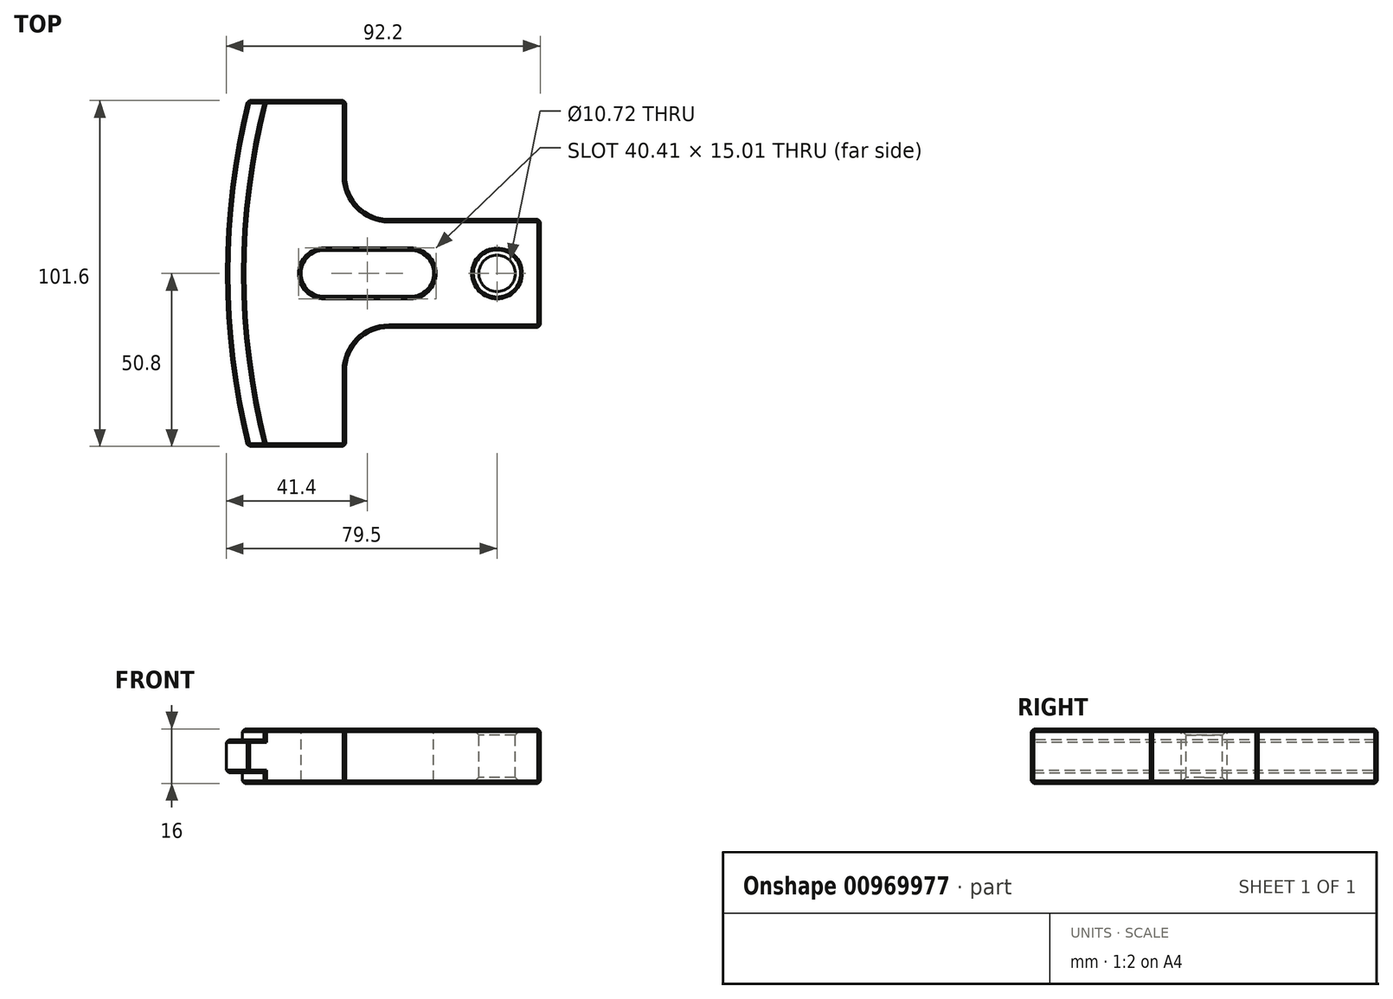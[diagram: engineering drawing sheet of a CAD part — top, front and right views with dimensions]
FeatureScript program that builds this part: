
annotation { "Feature Type Name" : "Feature", "Feature Type Description" : "" }
export const myFeature = defineFeature(function(context is Context, id is Id, definition is map)
    precondition{}
    {
        {
            var Q0;
            Q0=qCreatedBy(makeId("Top.planeOp"),FACE);
            var sketch = newSketch(context, id + "F0", { "sketchPlane" : qUnion([Q0])});
            skLineSegment(sketch, "E0", {"start": v(0, 0) * mm, "end": v(0, 15.88) * mm});
            skLineSegment(sketch, "E1", {"start": v(0, 15.88) * mm, "end": v(-44.45, 15.88) * mm});
            skLineSegment(sketch, "E2", {"start": v(-57.15, 28.57) * mm, "end": v(-57.15, 50.8) * mm});
            skLineSegment(sketch, "E3", {"start": v(-57.15, 50.8) * mm, "end": v(-85.9, 50.8) * mm});
            skLineSegment(sketch, "E4", {"start": v(-85.9, -50.8) * mm, "end": v(-57.15, -50.8) * mm});
            skLineSegment(sketch, "E5", {"start": v(-57.15, -50.8) * mm, "end": v(-57.15, -28.58) * mm});
            skLineSegment(sketch, "E6", {"start": v(-44.45, -15.88) * mm, "end": v(0, -15.88) * mm});
            skLineSegment(sketch, "E7", {"start": v(0, -15.88) * mm, "end": v(0, 0) * mm});
            skPoint(sketch, "E8", {"position": v(115.77, 0) * mm});
            skPoint(sketch, "E8.positionSnap0", {"position": v(-92.2, 0) * mm});
            skArc(sketch, "E9", {"start": v(-85.9, 50.8) * mm, "mid": v(-92.2, 0) * mm, "end": v(-85.9, -50.8) * mm});
            skPoint(sketch, "E10", {"position": v(-38.1, 0) * mm});
            skPoint(sketch, "E11", {"position": v(-63.5, 0) * mm});
            skCircle(sketch, "E12", {"center": v(-63.5, 0) * mm, "radius": 6.74 * mm});
            skCircle(sketch, "E13", {"center": v(-38.1, 0) * mm, "radius": 6.74 * mm});
            skLineSegment(sketch, "E14", {"start": v(-63.5, 6.74) * mm, "end": v(-38.1, 6.74) * mm});
            skLineSegment(sketch, "E15", {"start": v(-38.1, -6.74) * mm, "end": v(-63.5, -6.74) * mm});
            skPoint(sketch, "E16", {"position": v(-12.7, 0) * mm});
            skCircle(sketch, "E17", {"center": v(-12.7, 0) * mm, "radius": 5.36 * mm});
            skPoint(sketch, "E18.visualSharp", {"position": v(-57.15, 15.88) * mm});
            skArc(sketch, "E18.filletArc", {"start": v(-57.15, 28.57) * mm, "mid": v(-53.43, 19.6) * mm, "end": v(-44.45, 15.87) * mm});
            skPoint(sketch, "E19.visualSharp", {"position": v(-57.15, -15.88) * mm});
            skArc(sketch, "E19.filletArc", {"start": v(-44.45, -15.88) * mm, "mid": v(-53.43, -19.6) * mm, "end": v(-57.15, -28.57) * mm});
            skSolve(sketch);
        }
        {
            var Q0;
            Q0 = qSketchRegion(id + "F0", true);
            extrude(context, id + "F1", {"entities" : qUnion([Q0]), "oppositeDirection" : true, "depth" : 16 * mm, "offsetDistance" : 25.4 * mm});
        }
        {
            var Q0;
            Q0=makeQuery(id+"F1.opExtrude","SWEPT_FACE",FACE,{"disambiguationData":[OSD([sQuery(id+"F0.wireOp",EDGE,"E17")])]});
            chamfer(context, id + "F2", {"entities" : qUnion([Q0]), "width" : 1.78 * mm, "tangentPropagation" : true});
        }
        {
            var Q0;
            Q0=makeQuery(id+"F1.opExtrude","CAP_FACE",FACE,{"disambiguationData":[OSD([sQuery(id+"F0.wireOp",EDGE,"E0"),sQuery(id+"F0.wireOp",EDGE,"E1"),sQuery(id+"F0.wireOp",EDGE,"E2"),sQuery(id+"F0.wireOp",EDGE,"E3"),sQuery(id+"F0.wireOp",EDGE,"E4"),sQuery(id+"F0.wireOp",EDGE,"E5"),sQuery(id+"F0.wireOp",EDGE,"E6"),sQuery(id+"F0.wireOp",EDGE,"E7"),sQuery(id+"F0.wireOp",EDGE,"E9"),sQuery(id+"F0.wireOp",EDGE,"E12"),sQuery(id+"F0.wireOp",EDGE,"E13"),sQuery(id+"F0.wireOp",EDGE,"E14"),sQuery(id+"F0.wireOp",EDGE,"E15"),sQuery(id+"F0.wireOp",EDGE,"E17"),sQuery(id+"F0.wireOp",EDGE,"E18.filletArc"),sQuery(id+"F0.wireOp",EDGE,"E19.filletArc")])],"isStart":true});
            var sketch = newSketch(context, id + "F3", { "sketchPlane" : qUnion([Q0])});
            skCircle(sketch, "E20", {"center": v(115.77, 0) * mm, "radius": 203.2 * mm});
            skCircle(sketch, "E21", {"center": v(115.77, 0) * mm, "radius": 215.9 * mm});
            skSolve(sketch);
        }
        {
            var Q0;
            Q0 = qSketchRegion(id + "F3", true);
            extrude(context, id + "F4", {"entities" : qUnion([Q0]), "operationType" : NewBodyOperationType.REMOVE, "oppositeDirection" : true, "depth" : 3.17 * mm, "offsetDistance" : 25.4 * mm});
        }
        {
            var Q0;
            Q0=makeQuery(id+"F1.opExtrude","CAP_FACE",FACE,{"disambiguationData":[OSD([sQuery(id+"F0.wireOp",EDGE,"E0"),sQuery(id+"F0.wireOp",EDGE,"E1"),sQuery(id+"F0.wireOp",EDGE,"E2"),sQuery(id+"F0.wireOp",EDGE,"E3"),sQuery(id+"F0.wireOp",EDGE,"E4"),sQuery(id+"F0.wireOp",EDGE,"E5"),sQuery(id+"F0.wireOp",EDGE,"E6"),sQuery(id+"F0.wireOp",EDGE,"E7"),sQuery(id+"F0.wireOp",EDGE,"E9"),sQuery(id+"F0.wireOp",EDGE,"E12"),sQuery(id+"F0.wireOp",EDGE,"E13"),sQuery(id+"F0.wireOp",EDGE,"E14"),sQuery(id+"F0.wireOp",EDGE,"E15"),sQuery(id+"F0.wireOp",EDGE,"E17"),sQuery(id+"F0.wireOp",EDGE,"E18.filletArc"),sQuery(id+"F0.wireOp",EDGE,"E19.filletArc")])],"isStart":false});
            var sketch = newSketch(context, id + "F5", { "sketchPlane" : qUnion([Q0])});
            skCircle(sketch, "E22", {"center": v(115.77, 0) * mm, "radius": 203.2 * mm});
            skCircle(sketch, "E23", {"center": v(115.77, 0) * mm, "radius": 215.9 * mm});
            skSolve(sketch);
        }
        {
            var Q0;
            Q0 = qSketchRegion(id + "F5", true);
            extrude(context, id + "F6", {"entities" : qUnion([Q0]), "operationType" : NewBodyOperationType.REMOVE, "oppositeDirection" : true, "depth" : 3.17 * mm, "offsetDistance" : 25.4 * mm});
        }
        {
            var Q0;
            Q0=makeQuery(id+"F1.opExtrude","SWEPT_EDGE",EDGE,{"disambiguationData":[OSD([sQuery(id+"F0.wireOp",EDGE,"E4"),sQuery(id+"F0.wireOp",EDGE,"E9")])]});
            var Q1;
            Q1=makeQuery(id+"F6.boolean.opBoolean","INTERSECT",EDGE,{"derivedFrom":[makeQuery(id+"F1.opExtrude","SWEPT_FACE",FACE,{"disambiguationData":[OSD([sQuery(id+"F0.wireOp",EDGE,"E4")])]}),makeQuery(id+"F6.opExtrude","SWEPT_FACE",FACE,{"disambiguationData":[OSD([sQuery(id+"F5.wireOp",EDGE,"E22")])]})]});
            var Q2;
            Q2=makeQuery(id+"F6.boolean.opBoolean","INTERSECT",EDGE,{"derivedFrom":[makeQuery(id+"F1.opExtrude","SWEPT_FACE",FACE,{"disambiguationData":[OSD([sQuery(id+"F0.wireOp",EDGE,"E4")])]}),makeQuery(id+"F6.opExtrude","CAP_FACE",FACE,{"disambiguationData":[OSD([sQuery(id+"F5.wireOp",EDGE,"E22"),sQuery(id+"F5.wireOp",EDGE,"E23")])],"isStart":false})]});
            var Q3;
            Q3=makeQuery(id+"F4.boolean.opBoolean","INTERSECT",EDGE,{"derivedFrom":[makeQuery(id+"F1.opExtrude","SWEPT_FACE",FACE,{"disambiguationData":[OSD([sQuery(id+"F0.wireOp",EDGE,"E4")])]}),makeQuery(id+"F4.opExtrude","CAP_FACE",FACE,{"disambiguationData":[OSD([sQuery(id+"F3.wireOp",EDGE,"E20"),sQuery(id+"F3.wireOp",EDGE,"E21")])],"isStart":false})]});
            var Q4;
            Q4=makeQuery(id+"F4.boolean.opBoolean","INTERSECT",EDGE,{"derivedFrom":[makeQuery(id+"F1.opExtrude","SWEPT_FACE",FACE,{"disambiguationData":[OSD([sQuery(id+"F0.wireOp",EDGE,"E4")])]}),makeQuery(id+"F4.opExtrude","SWEPT_FACE",FACE,{"disambiguationData":[OSD([sQuery(id+"F3.wireOp",EDGE,"E20")])]})]});
            var Q5;
            Q5=makeQuery(id+"F1.opExtrude","SWEPT_EDGE",EDGE,{"disambiguationData":[OSD([sQuery(id+"F0.wireOp",EDGE,"E4"),sQuery(id+"F0.wireOp",EDGE,"E5")])]});
            var Q6;
            Q6=makeQuery(id+"F1.opExtrude","SWEPT_EDGE",EDGE,{"disambiguationData":[OSD([sQuery(id+"F0.wireOp",EDGE,"E6"),sQuery(id+"F0.wireOp",EDGE,"E7")])]});
            var Q7;
            Q7=makeQuery(id+"F1.opExtrude","SWEPT_EDGE",EDGE,{"disambiguationData":[OSD([sQuery(id+"F0.wireOp",EDGE,"E0"),sQuery(id+"F0.wireOp",EDGE,"E1")])]});
            var Q8;
            Q8=makeQuery(id+"F1.opExtrude","SWEPT_EDGE",EDGE,{"disambiguationData":[OSD([sQuery(id+"F0.wireOp",EDGE,"E2"),sQuery(id+"F0.wireOp",EDGE,"E3")])]});
            var Q9;
            Q9=makeQuery(id+"F6.boolean.opBoolean","INTERSECT",EDGE,{"derivedFrom":[makeQuery(id+"F1.opExtrude","SWEPT_FACE",FACE,{"disambiguationData":[OSD([sQuery(id+"F0.wireOp",EDGE,"E3")])]}),makeQuery(id+"F6.opExtrude","SWEPT_FACE",FACE,{"disambiguationData":[OSD([sQuery(id+"F5.wireOp",EDGE,"E22")])]})]});
            var Q10;
            Q10=makeQuery(id+"F6.boolean.opBoolean","INTERSECT",EDGE,{"derivedFrom":[makeQuery(id+"F1.opExtrude","SWEPT_FACE",FACE,{"disambiguationData":[OSD([sQuery(id+"F0.wireOp",EDGE,"E3")])]}),makeQuery(id+"F6.opExtrude","CAP_FACE",FACE,{"disambiguationData":[OSD([sQuery(id+"F5.wireOp",EDGE,"E22"),sQuery(id+"F5.wireOp",EDGE,"E23")])],"isStart":false})]});
            var Q11;
            Q11=makeQuery(id+"F1.opExtrude","SWEPT_EDGE",EDGE,{"disambiguationData":[OSD([sQuery(id+"F0.wireOp",EDGE,"E3"),sQuery(id+"F0.wireOp",EDGE,"E9")])]});
            var Q12;
            Q12=makeQuery(id+"F4.boolean.opBoolean","INTERSECT",EDGE,{"derivedFrom":[makeQuery(id+"F1.opExtrude","SWEPT_FACE",FACE,{"disambiguationData":[OSD([sQuery(id+"F0.wireOp",EDGE,"E3")])]}),makeQuery(id+"F4.opExtrude","CAP_FACE",FACE,{"disambiguationData":[OSD([sQuery(id+"F3.wireOp",EDGE,"E20"),sQuery(id+"F3.wireOp",EDGE,"E21")])],"isStart":false})]});
            var Q13;
            Q13=makeQuery(id+"F4.boolean.opBoolean","INTERSECT",EDGE,{"derivedFrom":[makeQuery(id+"F1.opExtrude","SWEPT_FACE",FACE,{"disambiguationData":[OSD([sQuery(id+"F0.wireOp",EDGE,"E3")])]}),makeQuery(id+"F4.opExtrude","SWEPT_FACE",FACE,{"disambiguationData":[OSD([sQuery(id+"F3.wireOp",EDGE,"E20")])]})]});
            chamfer(context, id + "F7", {"entities" : qUnion([Q0, Q1, Q2, Q3, Q4, Q5, Q6, Q7, Q8, Q9, Q10, Q11, Q12, Q13]), "width" : 0.76 * mm, "tangentPropagation" : true});
        }
        {
            var Q0;
            Q0=makeQuery(id+"F1.opExtrude","CAP_FACE",FACE,{"disambiguationData":[OSD([sQuery(id+"F0.wireOp",EDGE,"E0"),sQuery(id+"F0.wireOp",EDGE,"E1"),sQuery(id+"F0.wireOp",EDGE,"E2"),sQuery(id+"F0.wireOp",EDGE,"E3"),sQuery(id+"F0.wireOp",EDGE,"E4"),sQuery(id+"F0.wireOp",EDGE,"E5"),sQuery(id+"F0.wireOp",EDGE,"E6"),sQuery(id+"F0.wireOp",EDGE,"E7"),sQuery(id+"F0.wireOp",EDGE,"E9"),sQuery(id+"F0.wireOp",EDGE,"E12"),sQuery(id+"F0.wireOp",EDGE,"E13"),sQuery(id+"F0.wireOp",EDGE,"E14"),sQuery(id+"F0.wireOp",EDGE,"E15"),sQuery(id+"F0.wireOp",EDGE,"E17"),sQuery(id+"F0.wireOp",EDGE,"E18.filletArc"),sQuery(id+"F0.wireOp",EDGE,"E19.filletArc")])],"isStart":true});
            var Q1;
            Q1=makeQuery(id+"F1.opExtrude","CAP_FACE",FACE,{"disambiguationData":[OSD([sQuery(id+"F0.wireOp",EDGE,"E0"),sQuery(id+"F0.wireOp",EDGE,"E1"),sQuery(id+"F0.wireOp",EDGE,"E2"),sQuery(id+"F0.wireOp",EDGE,"E3"),sQuery(id+"F0.wireOp",EDGE,"E4"),sQuery(id+"F0.wireOp",EDGE,"E5"),sQuery(id+"F0.wireOp",EDGE,"E6"),sQuery(id+"F0.wireOp",EDGE,"E7"),sQuery(id+"F0.wireOp",EDGE,"E9"),sQuery(id+"F0.wireOp",EDGE,"E12"),sQuery(id+"F0.wireOp",EDGE,"E13"),sQuery(id+"F0.wireOp",EDGE,"E14"),sQuery(id+"F0.wireOp",EDGE,"E15"),sQuery(id+"F0.wireOp",EDGE,"E17"),sQuery(id+"F0.wireOp",EDGE,"E18.filletArc"),sQuery(id+"F0.wireOp",EDGE,"E19.filletArc")])],"isStart":false});
            var Q2;
            Q2=makeQuery(id+"F4.boolean.opBoolean","INTERSECT",EDGE,{"derivedFrom":[makeQuery(id+"F1.opExtrude","SWEPT_FACE",FACE,{"disambiguationData":[OSD([sQuery(id+"F0.wireOp",EDGE,"E9")])]}),makeQuery(id+"F4.opExtrude","CAP_FACE",FACE,{"disambiguationData":[OSD([sQuery(id+"F3.wireOp",EDGE,"E20"),sQuery(id+"F3.wireOp",EDGE,"E21")])],"isStart":false})]});
            var Q3;
            Q3=makeQuery(id+"F6.boolean.opBoolean","INTERSECT",EDGE,{"derivedFrom":[makeQuery(id+"F1.opExtrude","SWEPT_FACE",FACE,{"disambiguationData":[OSD([sQuery(id+"F0.wireOp",EDGE,"E9")])]}),makeQuery(id+"F6.opExtrude","CAP_FACE",FACE,{"disambiguationData":[OSD([sQuery(id+"F5.wireOp",EDGE,"E22"),sQuery(id+"F5.wireOp",EDGE,"E23")])],"isStart":false})]});
            chamfer(context, id + "F8", {"entities" : qUnion([Q0, Q1, Q2, Q3]), "width" : 0.76 * mm, "tangentPropagation" : true});
        }
    });
